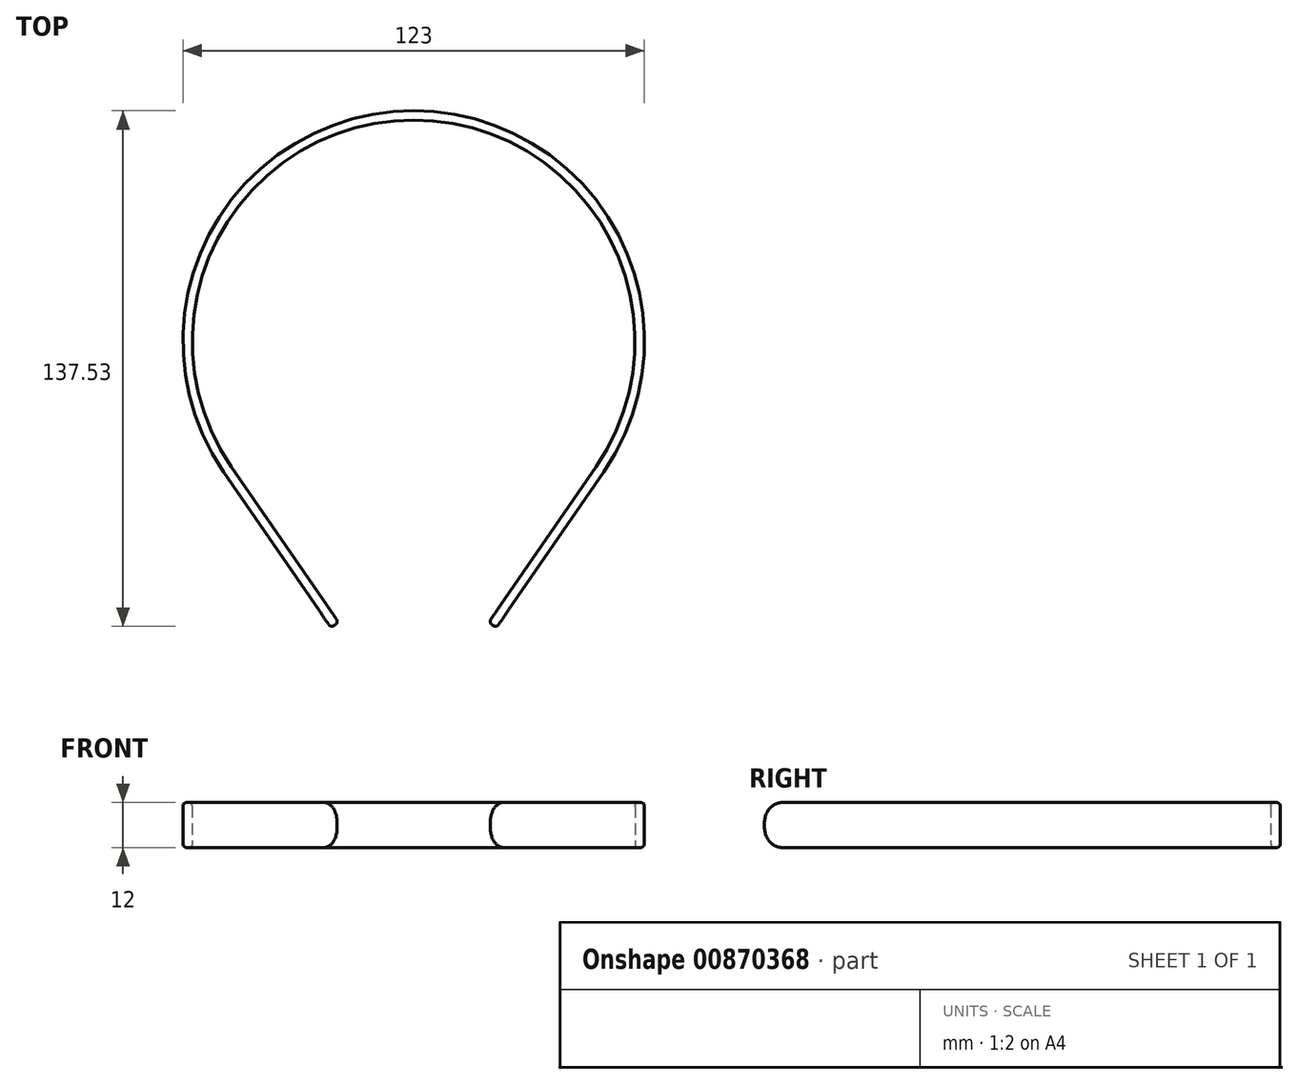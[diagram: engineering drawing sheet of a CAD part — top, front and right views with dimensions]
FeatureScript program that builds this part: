
annotation { "Feature Type Name" : "Feature", "Feature Type Description" : "" }
export const myFeature = defineFeature(function(context is Context, id is Id, definition is map)
    precondition{}
    {
        {
            var Q0;
            Q0=qCreatedBy(makeId("Top.planeOp"),FACE);
            var sketch = newSketch(context, id + "F0", { "sketchPlane" : qUnion([Q0])});
            skArc(sketch, "E0", {"start": v(48.6, -33.45) * mm, "mid": v(0, 59) * mm, "end": v(-48.6, -33.45) * mm});
            skLineSegment(sketch, "E1", {"start": v(-48.6, -33.45) * mm, "end": v(-20, -75) * mm});
            skLineSegment(sketch, "E2", {"start": v(48.6, -33.45) * mm, "end": v(20, -75) * mm});
            skArc(sketch, "E3.0", {"start": v(50.66, -34.87) * mm, "mid": v(0, 61.5) * mm, "end": v(-50.66, -34.87) * mm});
            skLineSegment(sketch, "E4.0", {"start": v(-50.66, -34.87) * mm, "end": v(-22.06, -76.42) * mm});
            skPoint(sketch, "E5.orphan", {"position": v(-74.66, 0) * mm});
            skLineSegment(sketch, "E6.0", {"start": v(50.66, -34.87) * mm, "end": v(22.06, -76.42) * mm});
            skPoint(sketch, "E7.orphan", {"position": v(0, -61.5) * mm});
            skLineSegment(sketch, "E8", {"start": v(-22.06, -76.42) * mm, "end": v(-20, -75) * mm});
            skLineSegment(sketch, "E9", {"start": v(22.06, -76.42) * mm, "end": v(20, -75) * mm});
            skSolve(sketch);
        }
        {
            var Q0;
            Q0 = qSketchRegion(id + "F0", true);
            extrude(context, id + "F1", {"entities" : qUnion([Q0]), "depth" : 12 * mm, "offsetDistance" : 25 * mm});
        }
        {
            var Q0;
            Q0=makeQuery(id+"F1.opExtrude","CAP_EDGE",EDGE,{"disambiguationData":[OSD([sQuery(id+"F0.wireOp",EDGE,"E8")])],"isStart":true});
            var Q1;
            Q1=makeQuery(id+"F1.opExtrude","CAP_EDGE",EDGE,{"disambiguationData":[OSD([sQuery(id+"F0.wireOp",EDGE,"E8")])],"isStart":false});
            var Q2;
            Q2=makeQuery(id+"F1.opExtrude","CAP_EDGE",EDGE,{"disambiguationData":[OSD([sQuery(id+"F0.wireOp",EDGE,"E9")])],"isStart":false});
            var Q3;
            Q3=makeQuery(id+"F1.opExtrude","CAP_EDGE",EDGE,{"disambiguationData":[OSD([sQuery(id+"F0.wireOp",EDGE,"E9")])],"isStart":true});
            fillet(context, id + "F2", {"entities" : qUnion([Q0, Q1, Q2, Q3]), "radius" : 5.5 * mm, "tangentPropagation" : true, "allowEdgeOverflow" : false});
        }
        {
            var Q0;
            Q0=makeQuery(id+"F1.opExtrude","CAP_EDGE",EDGE,{"disambiguationData":[OSD([sQuery(id+"F0.wireOp",EDGE,"E4.0")])],"isStart":false});
            var Q1;
            Q1=makeQuery(id+"F1.opExtrude","CAP_EDGE",EDGE,{"disambiguationData":[OSD([sQuery(id+"F0.wireOp",EDGE,"E1")])],"isStart":true});
            fillet(context, id + "F3", {"entities" : qUnion([Q0, Q1]), "radius" : 1 * mm, "tangentPropagation" : true, "allowEdgeOverflow" : false});
        }
    });
